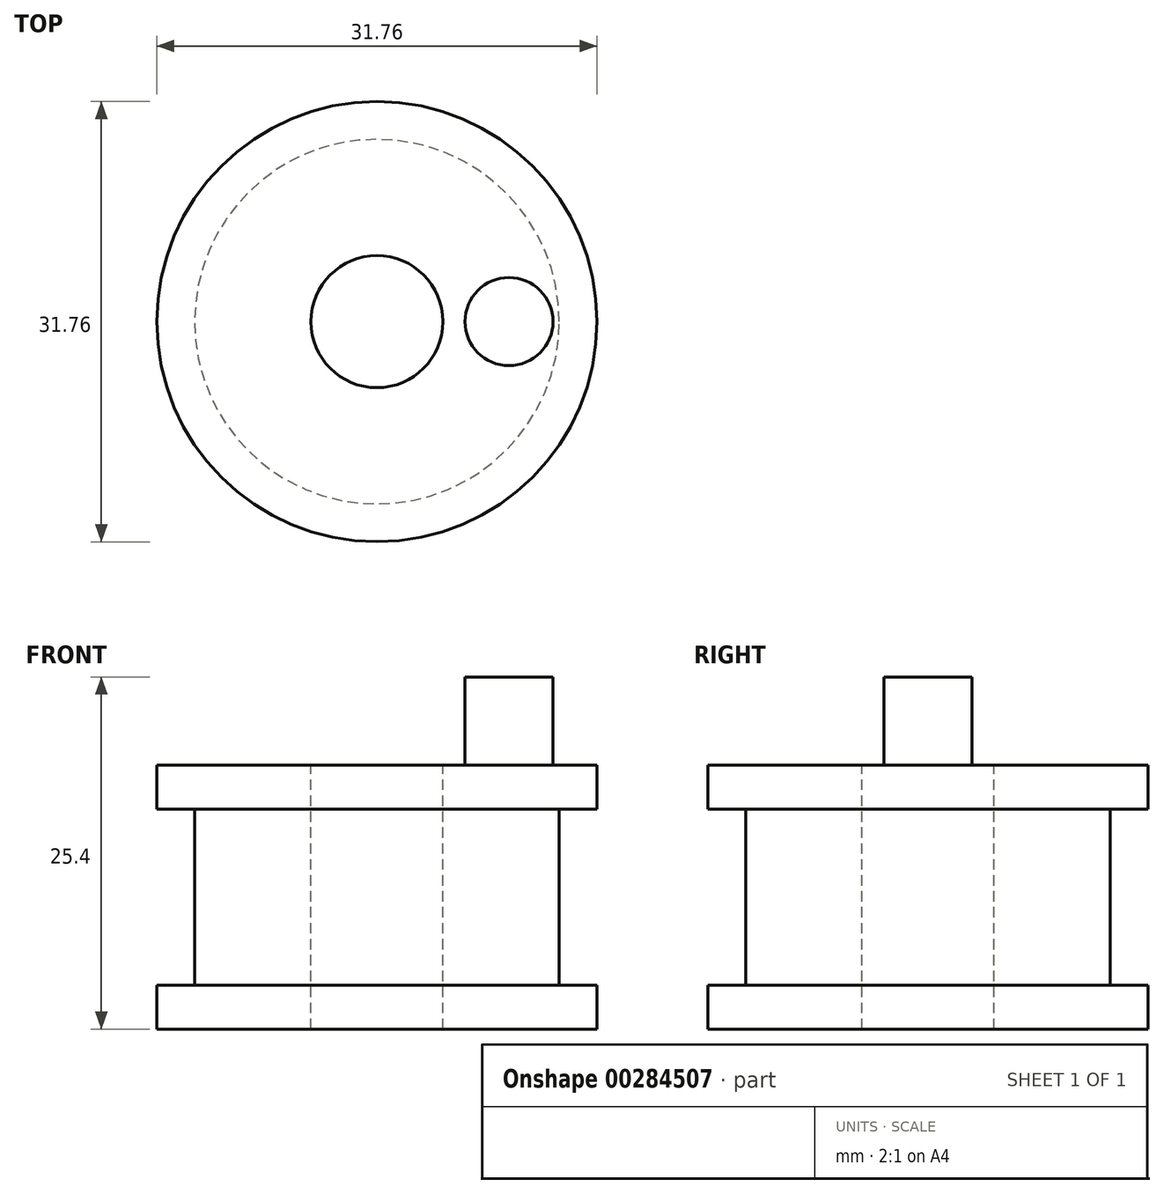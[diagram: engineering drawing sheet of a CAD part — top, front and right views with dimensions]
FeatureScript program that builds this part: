
annotation { "Feature Type Name" : "Feature", "Feature Type Description" : "" }
export const myFeature = defineFeature(function(context is Context, id is Id, definition is map)
    precondition{}
    {
        {
            var Q0;
            Q0=qCreatedBy(makeId("Front.planeOp"),FACE);
            var sketch = newSketch(context, id + "F0", { "sketchPlane" : qUnion([Q0])});
            skLineSegment(sketch, "E0", {"start": v(15.88, 0) * mm, "end": v(15.88, -3.17) * mm});
            skLineSegment(sketch, "E1", {"start": v(15.88, -3.18) * mm, "end": v(13.15, -3.18) * mm});
            skLineSegment(sketch, "E2", {"start": v(13.15, -3.18) * mm, "end": v(13.15, -15.88) * mm});
            skLineSegment(sketch, "E3", {"start": v(13.15, -15.88) * mm, "end": v(15.88, -15.88) * mm});
            skLineSegment(sketch, "E4", {"start": v(15.88, -15.88) * mm, "end": v(15.88, -19.05) * mm});
            skLineSegment(sketch, "E5", {"start": v(0, 0) * mm, "end": v(4.76, 0) * mm});
            skLineSegment(sketch, "E6", {"start": v(15.88, 0) * mm, "end": v(4.76, 0) * mm});
            skLineSegment(sketch, "E7", {"start": v(15.88, -19.05) * mm, "end": v(4.76, -19.05) * mm});
            skLineSegment(sketch, "E8", {"start": v(4.76, 0) * mm, "end": v(4.76, -19.05) * mm});
            skLineSegment(sketch, "E9", {"start": v(0, 0) * mm, "end": v(0, -19.05) * mm});
            skSolve(sketch);
        }
        {
            var Q0;
            Q0 = qSketchRegion(id + "F0", true);
            var Q1;
            Q1=sQuery(id+"F0.wireOp",EDGE,"E9");
            revolve(context, id + "F1", {"entities" : qUnion([Q0]), "axis" : qUnion([Q1]), "revolveType" : RevolveType.FULL});
        }
        {
            var Q0;
            Q0=qCreatedBy(makeId("Top.planeOp"),FACE);
            var sketch = newSketch(context, id + "F2", { "sketchPlane" : qUnion([Q0])});
            skLineSegment(sketch, "E10", {"start": v(0, 0) * mm, "end": v(9.53, 0) * mm});
            skCircle(sketch, "E11", {"center": v(9.53, 0) * mm, "radius": 3.18 * mm});
            skSolve(sketch);
        }
        {
            var Q0;
            Q0=makeQuery(id+"F2.imprint","IMPRINT",FACE,{"disambiguationData":[TD([[makeQuery(id+"F2.imprint","IMPRINT",EDGE,{"derivedFrom":sQuery(id+"F2.wireOp",EDGE,"E11")}),1.0]])]});
            extrude(context, id + "F3", {"entities" : qUnion([Q0]), "operationType" : NewBodyOperationType.ADD, "depth" : 6.35 * mm});
        }
    });
